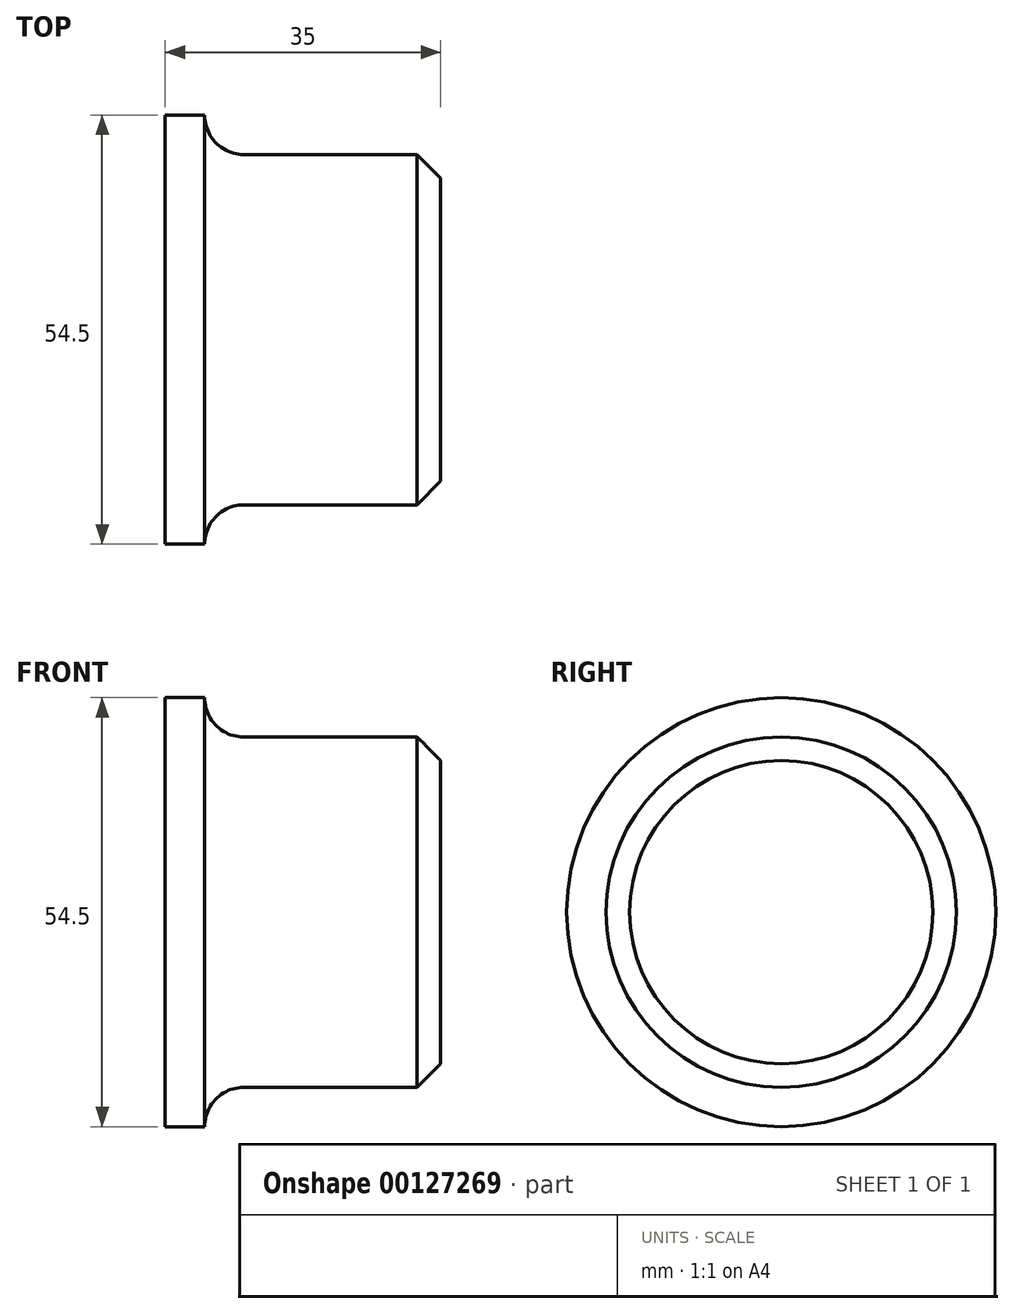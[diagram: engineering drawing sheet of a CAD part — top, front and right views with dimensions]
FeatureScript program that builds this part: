
annotation { "Feature Type Name" : "Feature", "Feature Type Description" : "" }
export const myFeature = defineFeature(function(context is Context, id is Id, definition is map)
    precondition{}
    {
        {
            var Q0;
            Q0=qCreatedBy(makeId("Front.planeOp"),FACE);
            var sketch = newSketch(context, id + "F0", { "sketchPlane" : qUnion([Q0])});
            skPoint(sketch, "E0", {"position": v(0, 0) * mm});
            skLineSegment(sketch, "E1", {"start": v(0, 0) * mm, "end": v(-94, 0) * mm, "construction": true});
            skPoint(sketch, "E2", {"position": v(-44, 0) * mm});
            skPoint(sketch, "E3", {"position": v(-64, 0) * mm});
            skLineSegment(sketch, "E4", {"start": v(-94, 0) * mm, "end": v(-94, 22.25) * mm, "construction": true});
            skPoint(sketch, "E5", {"position": v(-64, 22.25) * mm});
            skLineSegment(sketch, "E6", {"start": v(-94, 22.25) * mm, "end": v(-64, 22.25) * mm});
            skPoint(sketch, "E7", {"position": v(-94, 27.25) * mm});
            skLineSegment(sketch, "E8", {"start": v(-94, 22.25) * mm, "end": v(-94, 27.25) * mm});
            skLineSegment(sketch, "E9", {"start": v(-94, 27.25) * mm, "end": v(-99, 27.25) * mm});
            skLineSegment(sketch, "E10", {"start": v(-64, 22.25) * mm, "end": v(-64, 0) * mm});
            skLineSegment(sketch, "E11", {"start": v(-99, 27.25) * mm, "end": v(-99, 0) * mm});
            skLineSegment(sketch, "E12", {"start": v(-99, 0) * mm, "end": v(-64, 0) * mm});
            skSolve(sketch);
        }
        {
            var Q0;
            Q0=makeQuery(id+"F0.imprint","IMPRINT",FACE,{"disambiguationData":[TD([[makeQuery(id+"F0.imprint","IMPRINT",EDGE,{"derivedFrom":sQuery(id+"F0.wireOp",EDGE,"E6")}),-1.0]])]});
            var Q1;
            Q1=sQuery(id+"F0.wireOp",EDGE,"E1");
            revolve(context, id + "F1", {"entities" : qUnion([Q0]), "axis" : qUnion([Q1]), "revolveType" : RevolveType.FULL});
        }
        {
            var Q0;
            Q0=makeQuery(id+"F1.opRevolve","SWEPT_EDGE",EDGE,{"disambiguationData":[OSD([sQuery(id+"F0.wireOp",EDGE,"E6"),sQuery(id+"F0.wireOp",EDGE,"E10")])]});
            chamfer(context, id + "F2", {"entities" : qUnion([Q0]), "width" : 3 * mm, "tangentPropagation" : true});
        }
        {
            var Q0;
            Q0=makeQuery(id+"F1.opRevolve","SWEPT_EDGE",EDGE,{"disambiguationData":[OSD([sQuery(id+"F0.wireOp",EDGE,"E6"),sQuery(id+"F0.wireOp",EDGE,"E8")])]});
            fillet(context, id + "F3", {"entities" : qUnion([Q0]), "radius" : 5 * mm, "tangentPropagation" : true, "allowEdgeOverflow" : false});
        }
    });
